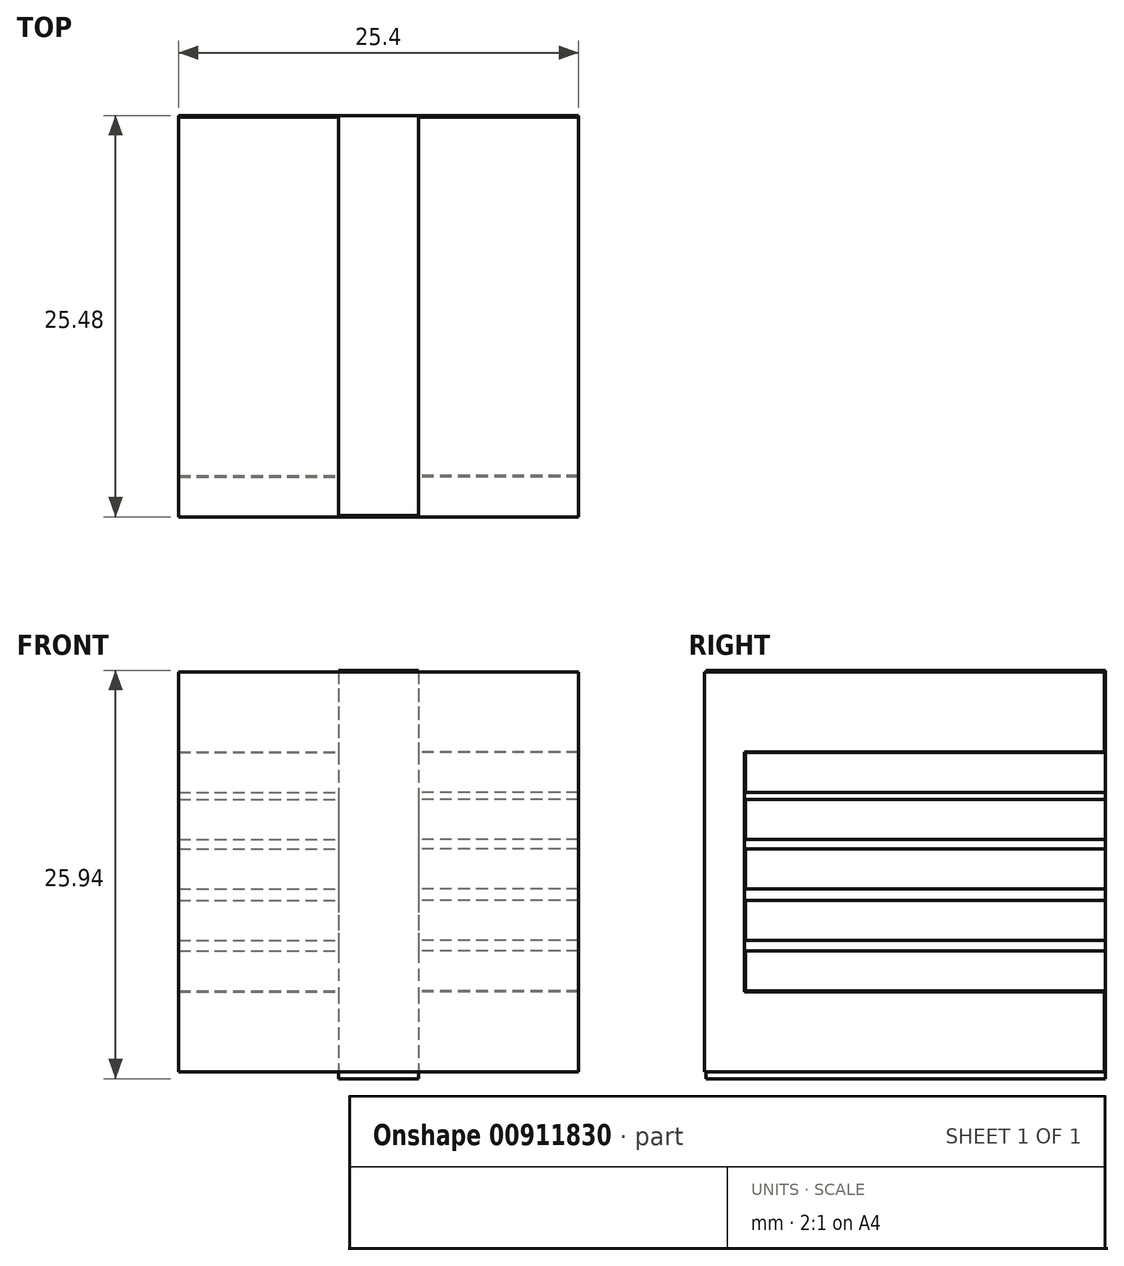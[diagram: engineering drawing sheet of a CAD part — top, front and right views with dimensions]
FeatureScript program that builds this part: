
annotation { "Feature Type Name" : "Feature", "Feature Type Description" : "" }
export const myFeature = defineFeature(function(context is Context, id is Id, definition is map)
    precondition{}
    {
        {
            var Q0;
            Q0=qCreatedBy(makeId("Right.planeOp"),FACE);
            var sketch = newSketch(context, id + "F0", { "sketchPlane" : qUnion([Q0])});
            skLineSegment(sketch, "E0", {"start": v(-12.64, -12.27) * mm, "end": v(-12.64, 13.13) * mm});
            skLineSegment(sketch, "E1", {"start": v(12.76, 13.13) * mm, "end": v(-12.64, 13.13) * mm});
            skLineSegment(sketch, "E2", {"start": v(12.76, 13.13) * mm, "end": v(12.76, 8.05) * mm});
            skLineSegment(sketch, "E3", {"start": v(12.76, 8.05) * mm, "end": v(-10.1, 8.05) * mm});
            skLineSegment(sketch, "E4", {"start": v(-10.1, 8.05) * mm, "end": v(-10.1, -7.2) * mm});
            skLineSegment(sketch, "E5", {"start": v(-10.1, -7.2) * mm, "end": v(12.76, -7.2) * mm});
            skLineSegment(sketch, "E6", {"start": v(12.76, -7.2) * mm, "end": v(12.76, -12.27) * mm});
            skLineSegment(sketch, "E7", {"start": v(12.76, -12.27) * mm, "end": v(-12.64, -12.27) * mm});
            skSolve(sketch);
        }
        {
            var Q0;
            Q0 = qSketchRegion(id + "F0", true);
            extrude(context, id + "F1", {"entities" : qUnion([Q0]), "depth" : 12.7 * mm, "offsetDistance" : 25.4 * mm});
        }
        {
            var Q0;
            Q0=qCreatedBy(makeId("Right.planeOp"),FACE);
            var sketch = newSketch(context, id + "F2", { "sketchPlane" : qUnion([Q0])});
            skLineSegment(sketch, "E8.bottom", {"start": v(12.84, 8) * mm, "end": v(-10.02, 8) * mm});
            skLineSegment(sketch, "E8.top", {"start": v(12.84, 5.47) * mm, "end": v(-10.02, 5.47) * mm});
            skLineSegment(sketch, "E8.left", {"start": v(12.84, 8) * mm, "end": v(12.84, 5.47) * mm});
            skLineSegment(sketch, "E8.right", {"start": v(-10.02, 8) * mm, "end": v(-10.02, 5.47) * mm});
            skLineSegment(sketch, "E9.bottom", {"start": v(12.84, 5.02) * mm, "end": v(-10.02, 5.02) * mm});
            skLineSegment(sketch, "E9.top", {"start": v(12.84, 2.48) * mm, "end": v(-10.02, 2.48) * mm});
            skLineSegment(sketch, "E9.left", {"start": v(12.84, 5.02) * mm, "end": v(12.84, 2.48) * mm});
            skLineSegment(sketch, "E9.right", {"start": v(-10.02, 5.02) * mm, "end": v(-10.02, 2.48) * mm});
            skLineSegment(sketch, "E10.bottom", {"start": v(12.84, 1.9) * mm, "end": v(-10.02, 1.9) * mm});
            skLineSegment(sketch, "E10.top", {"start": v(12.84, -0.65) * mm, "end": v(-10.02, -0.65) * mm});
            skLineSegment(sketch, "E10.left", {"start": v(12.84, 1.9) * mm, "end": v(12.84, -0.65) * mm});
            skLineSegment(sketch, "E10.right", {"start": v(-10.02, 1.9) * mm, "end": v(-10.02, -0.65) * mm});
            skLineSegment(sketch, "E11.bottom", {"start": v(12.84, -1.39) * mm, "end": v(-10.02, -1.39) * mm});
            skLineSegment(sketch, "E11.top", {"start": v(12.84, -3.93) * mm, "end": v(-10.02, -3.93) * mm});
            skLineSegment(sketch, "E11.left", {"start": v(12.84, -1.39) * mm, "end": v(12.84, -3.93) * mm});
            skLineSegment(sketch, "E11.right", {"start": v(-10.02, -1.39) * mm, "end": v(-10.02, -3.93) * mm});
            skLineSegment(sketch, "E12.bottom", {"start": v(12.84, -4.6) * mm, "end": v(-10.02, -4.6) * mm});
            skLineSegment(sketch, "E12.top", {"start": v(12.84, -7.14) * mm, "end": v(-10.02, -7.14) * mm});
            skLineSegment(sketch, "E12.left", {"start": v(12.84, -4.6) * mm, "end": v(12.84, -7.14) * mm});
            skLineSegment(sketch, "E12.right", {"start": v(-10.02, -4.6) * mm, "end": v(-10.02, -7.14) * mm});
            skSolve(sketch);
        }
        {
            var Q0;
            Q0 = qSketchRegion(id + "F2", true);
            extrude(context, id + "F3", {"entities" : qUnion([Q0]), "operationType" : NewBodyOperationType.ADD, "depth" : 12.7 * mm, "offsetDistance" : 25.4 * mm});
        }
        {
            var Q0;
            Q0=qCreatedBy(makeId("Right.planeOp"),FACE);
            var sketch = newSketch(context, id + "F4", { "sketchPlane" : qUnion([Q0])});
            skLineSegment(sketch, "E13.bottom", {"start": v(-12.56, 13.23) * mm, "end": v(12.83, 13.23) * mm});
            skLineSegment(sketch, "E13.top", {"start": v(-12.56, -12.7) * mm, "end": v(12.83, -12.7) * mm});
            skLineSegment(sketch, "E13.left", {"start": v(-12.56, 13.23) * mm, "end": v(-12.56, -12.7) * mm});
            skLineSegment(sketch, "E13.right", {"start": v(12.83, 13.23) * mm, "end": v(12.83, -12.7) * mm});
            skSolve(sketch);
        }
        {
            var Q0;
            Q0 = qSketchRegion(id + "F4", true);
            extrude(context, id + "F5", {"entities" : qUnion([Q0]), "operationType" : NewBodyOperationType.ADD, "depth" : 2.54 * mm, "offsetDistance" : 25.4 * mm});
        }
        {
            var Q0;
            Q0=makeQuery(id+"F1.opExtrude","SWEPT_BODY",BODY,{"disambiguationData":[OSD([sQuery(id+"F0.wireOp",EDGE,"E0"),sQuery(id+"F0.wireOp",EDGE,"E1"),sQuery(id+"F0.wireOp",EDGE,"E2"),sQuery(id+"F0.wireOp",EDGE,"E3"),sQuery(id+"F0.wireOp",EDGE,"E4"),sQuery(id+"F0.wireOp",EDGE,"E5"),sQuery(id+"F0.wireOp",EDGE,"E6"),sQuery(id+"F0.wireOp",EDGE,"E7")])]});
            var Q1;
            Q1=qCreatedBy(makeId("Right.planeOp"),FACE);
            mirror(context, id + "F6", {"operationType" : NewBodyOperationType.ADD, "entities" : qUnion([Q0]), "mirrorPlane" : qUnion([Q1])});
        }
    });
